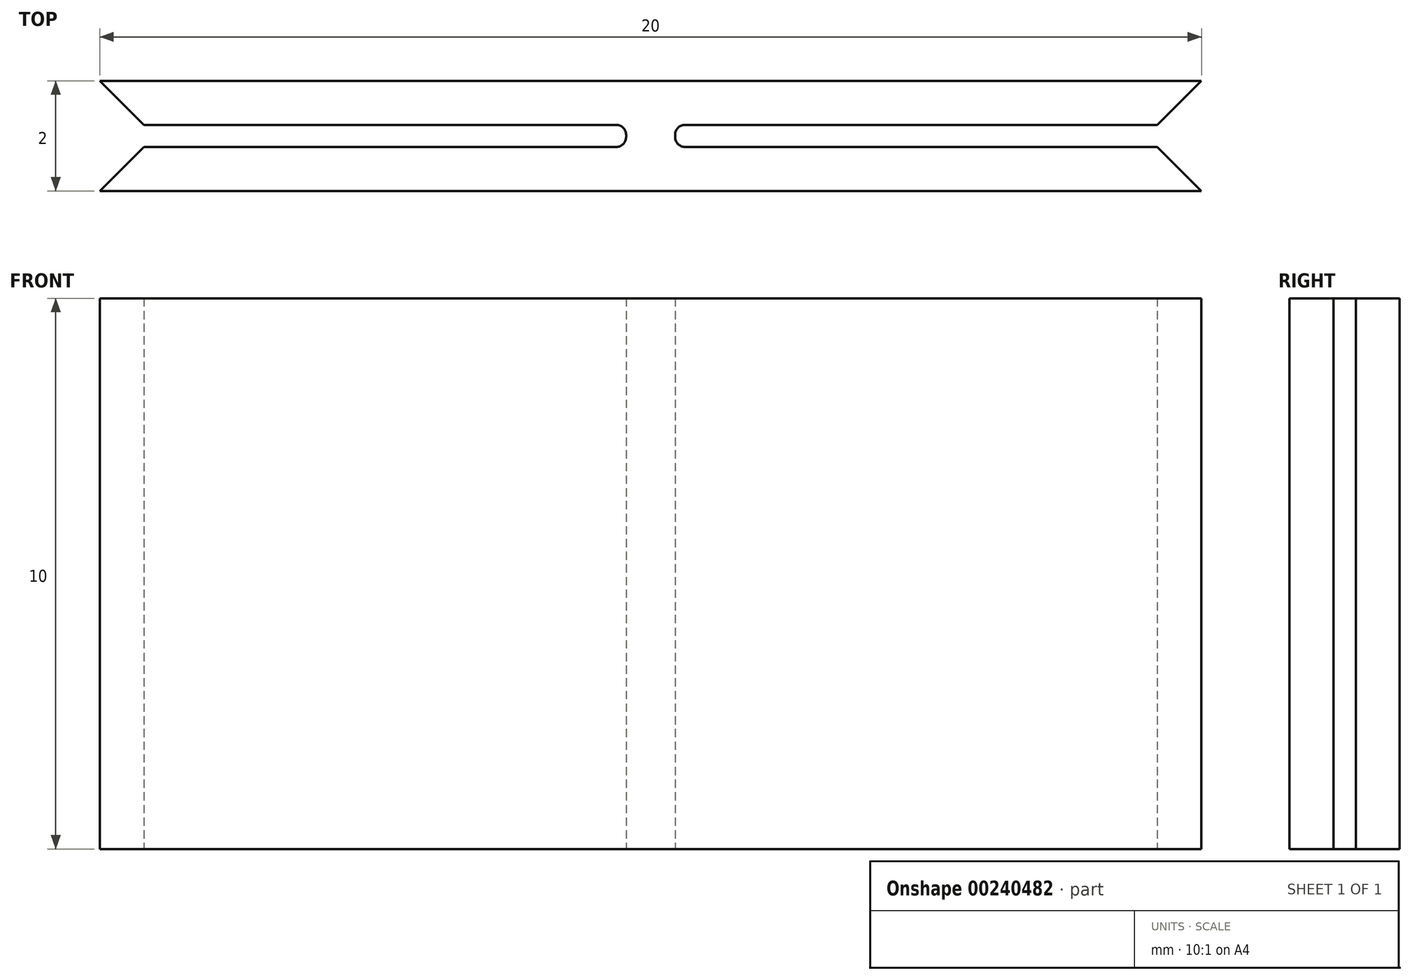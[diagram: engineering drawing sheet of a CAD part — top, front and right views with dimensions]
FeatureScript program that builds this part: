
annotation { "Feature Type Name" : "Feature", "Feature Type Description" : "" }
export const myFeature = defineFeature(function(context is Context, id is Id, definition is map)
    precondition{}
    {
        {
            var Q0;
            Q0=qCreatedBy(makeId("Top.planeOp"),FACE);
            var sketch = newSketch(context, id + "F0", { "sketchPlane" : qUnion([Q0])});
            skLineSegment(sketch, "E0.bottom", {"start": v(10, 1) * mm, "end": v(-10, 1) * mm});
            skLineSegment(sketch, "E0.top", {"start": v(10, -1) * mm, "end": v(-10, -1) * mm});
            skLineSegment(sketch, "E0.left", {"start": v(10, 1) * mm, "end": v(10, 0.2) * mm});
            skLineSegment(sketch, "E0.right", {"start": v(-10, 1) * mm, "end": v(-10, 0.2) * mm});
            skPoint(sketch, "E0.middle", {"position": v(0, 0) * mm});
            skLineSegment(sketch, "E1.bottom", {"start": v(10, 0.2) * mm, "end": v(0.44, 0.2) * mm});
            skLineSegment(sketch, "E1.top", {"start": v(10, -0.2) * mm, "end": v(0.44, -0.2) * mm});
            skLineSegment(sketch, "E2.bottom", {"start": v(0.44, 1) * mm, "end": v(-0.44, 1) * mm});
            skLineSegment(sketch, "E2.top", {"start": v(0.44, -1) * mm, "end": v(-0.44, -1) * mm});
            skLineSegment(sketch, "E2.left", {"start": v(0.44, 0.2) * mm, "end": v(0.44, -0.2) * mm});
            skLineSegment(sketch, "E2.right", {"start": v(-0.44, 0.2) * mm, "end": v(-0.44, -0.2) * mm});
            skLineSegment(sketch, "E3.trimOffspring", {"start": v(-10, -0.2) * mm, "end": v(-10, -1) * mm});
            skLineSegment(sketch, "E4.trimOffspring", {"start": v(10, -0.2) * mm, "end": v(10, -1) * mm});
            skLineSegment(sketch, "E5.trimOffspring", {"start": v(-0.44, 0.2) * mm, "end": v(-10, 0.2) * mm});
            skLineSegment(sketch, "E6.trimOffspring", {"start": v(-0.44, -0.2) * mm, "end": v(-10, -0.2) * mm});
            skSolve(sketch);
        }
        {
            var Q0;
            {var subQ0=sQuery(id+"F0.wireOp",EDGE,"E0.left");Q0=makeQuery(id+"F0.imprint","IMPRINT",FACE,{"disambiguationData":[TD([[makeQuery(id+"F0.imprint","IMPRINT",EDGE,{"derivedFrom":subQ0}),-1.0]])]});}
            extrude(context, id + "F1", {"entities" : qUnion([Q0]), "depth" : 10 * mm});
        }
        {
            var Q0;
            Q0=makeQuery(id+"F1.opExtrude","SWEPT_EDGE",EDGE,{"disambiguationData":[OSD([sQuery(id+"F0.wireOp",EDGE,"E3.trimOffspring"),sQuery(id+"F0.wireOp",EDGE,"E6.trimOffspring")])]});
            var Q1;
            Q1=makeQuery(id+"F1.opExtrude","SWEPT_EDGE",EDGE,{"disambiguationData":[OSD([sQuery(id+"F0.wireOp",EDGE,"E0.right"),sQuery(id+"F0.wireOp",EDGE,"E5.trimOffspring")])]});
            var Q2;
            Q2=makeQuery(id+"F1.opExtrude","SWEPT_EDGE",EDGE,{"disambiguationData":[OSD([sQuery(id+"F0.wireOp",EDGE,"E1.top"),sQuery(id+"F0.wireOp",EDGE,"E4.trimOffspring")])]});
            var Q3;
            Q3=makeQuery(id+"F1.opExtrude","SWEPT_EDGE",EDGE,{"disambiguationData":[OSD([sQuery(id+"F0.wireOp",EDGE,"E0.left"),sQuery(id+"F0.wireOp",EDGE,"E1.bottom")])]});
            chamfer(context, id + "F2", {"entities" : qUnion([Q0, Q1, Q2, Q3]), "width" : .8 * mm, "tangentPropagation" : true});
        }
        {
            var Q0;
            Q0=makeQuery(id+"F1.opExtrude","SWEPT_EDGE",EDGE,{"disambiguationData":[OSD([sQuery(id+"F0.wireOp",EDGE,"E2.right"),sQuery(id+"F0.wireOp",EDGE,"E6.trimOffspring")])]});
            var Q1;
            Q1=makeQuery(id+"F1.opExtrude","SWEPT_EDGE",EDGE,{"disambiguationData":[OSD([sQuery(id+"F0.wireOp",EDGE,"E2.right"),sQuery(id+"F0.wireOp",EDGE,"E5.trimOffspring")])]});
            var Q2;
            Q2=makeQuery(id+"F1.opExtrude","SWEPT_EDGE",EDGE,{"disambiguationData":[OSD([sQuery(id+"F0.wireOp",EDGE,"E1.bottom"),sQuery(id+"F0.wireOp",EDGE,"E2.left")])]});
            var Q3;
            Q3=makeQuery(id+"F1.opExtrude","SWEPT_EDGE",EDGE,{"disambiguationData":[OSD([sQuery(id+"F0.wireOp",EDGE,"E1.top"),sQuery(id+"F0.wireOp",EDGE,"E2.left")])]});
            fillet(context, id + "F3", {"entities" : qUnion([Q0, Q1, Q2, Q3]), "radius" : .18 * mm, "tangentPropagation" : true, "allowEdgeOverflow" : false});
        }
    });
